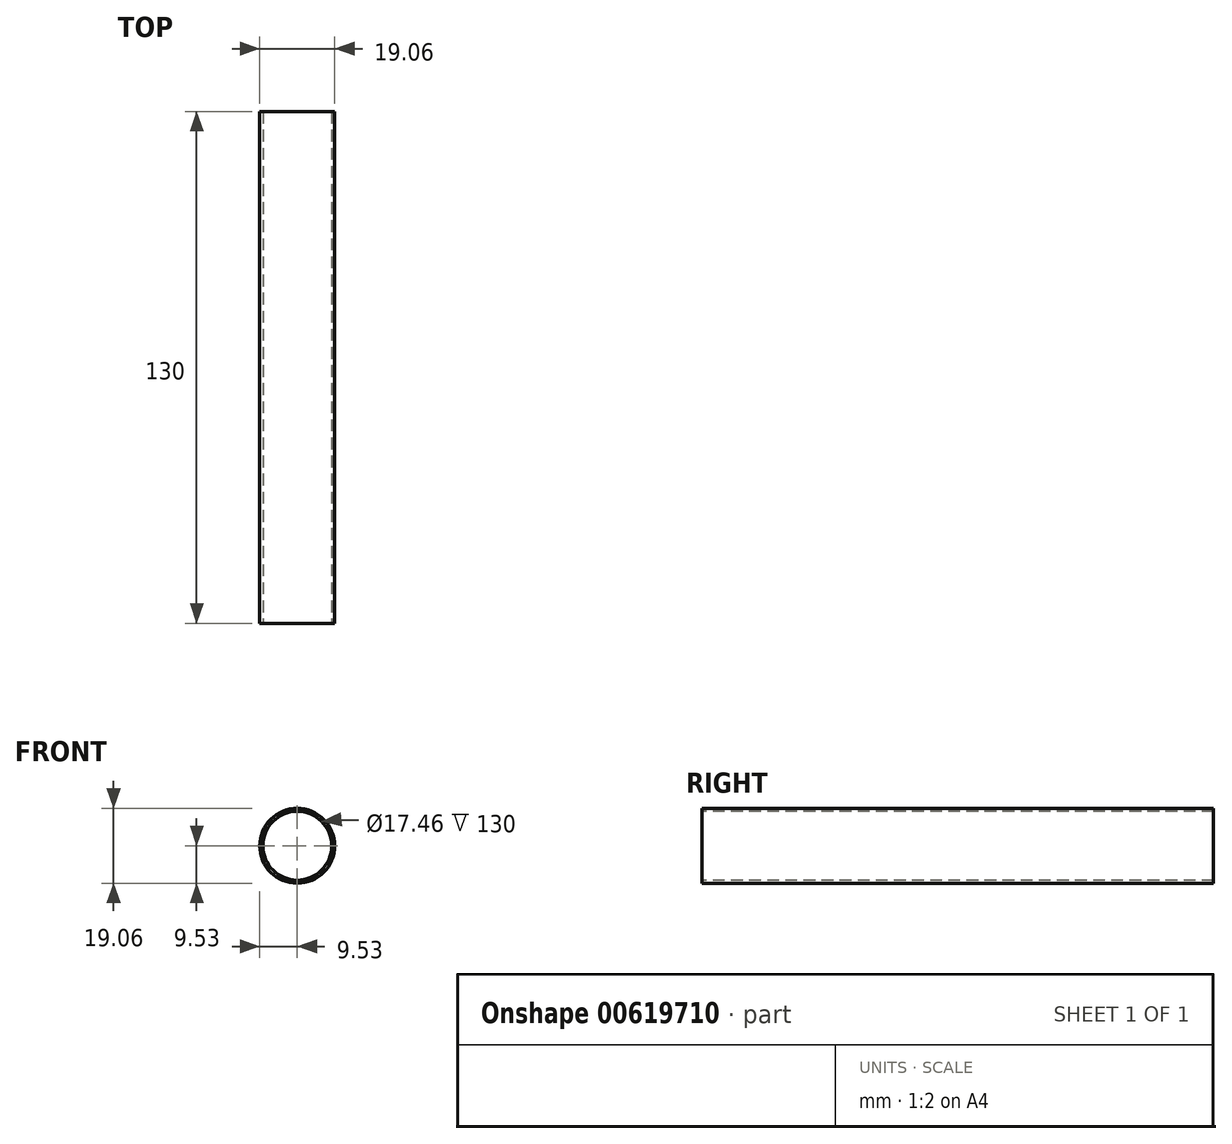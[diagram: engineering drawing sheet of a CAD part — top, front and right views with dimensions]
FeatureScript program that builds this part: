
annotation { "Feature Type Name" : "Feature", "Feature Type Description" : "" }
export const myFeature = defineFeature(function(context is Context, id is Id, definition is map)
    precondition{}
    {
        {
            var Q0;
            Q0=qCreatedBy(makeId("Front.planeOp"),FACE);
            var sketch = newSketch(context, id + "F0", { "sketchPlane" : qUnion([Q0])});
            skCircle(sketch, "E0", {"center": v(0, 0) * mm, "radius": 9.53 * mm});
            skCircle(sketch, "E1", {"center": v(0, 0) * mm, "radius": 8.73 * mm});
            skSolve(sketch);
        }
        {
            var Q0;
            Q0=makeQuery(id+"F0.imprint","IMPRINT",FACE,{"disambiguationData":[TD([[makeQuery(id+"F0.imprint","IMPRINT",EDGE,{"derivedFrom":sQuery(id+"F0.wireOp",EDGE,"E0")}),1.0]])]});
            extrude(context, id + "F1", {"entities" : qUnion([Q0]), "endBound" : BoundingType.SYMMETRIC, "oppositeDirection" : true, "depth" : 130 * mm, "offsetDistance" : 25.4 * mm});
        }
    });
